# Revit family: 706510001_Dispensador de Toallas
name_source: partatom
category: Generic Models
units: mm (PartAtom-declared; Revit-internal decimal feet)

## family parameters
Always vertical = Yes
Can host rebar = No
Cut with Voids When Loaded = No
Host = Wall
OmniClass Number = 23.31.25.19.13
OmniClass Title = Paper Towel Dispenser With Disposal Units
Part Type = Normal
Room Calculation Point = No
Round Connector Dimension = Use Diameter
Shared = No

## types (1)
- Ref. 706510001 Dispensador de Toallas
    Acabado = Cromado
    Alto = 260 mm  [stored 0.853018 ft]
    Ancho = 282 mm  [stored 0.925197 ft]
    Años de Garantía = 1 año
    Capacidad de toallas doblez sencillo = 150
    Capacidad de toallas pleglables = 200
    Creado por = IDD
    Description = Tamaño ajustado para adecuar en diferentes baños
• Visor de nivel de toallas para abastecimiento.
• Cerradura de llave (incluye juegos para mantenimiento).
• Sistema de fijación extrema, ideal para instituciones de alto tráfico.
• Fabricación en acero inoxidable ofreciendo mayor calidad y servicio.
    Dimensiones generales del producto = Largo (cm) 280 ancho (cm)
102 alto (cm) 248.
    Fecha de creación = 22/07/2020
    Garantía Acabados = 3 años
    Manufacturer = Corona
    Material = Corona_Acero inoxidable
    Peso Bruto aprox = 1,660 g 3.6597 lb
    Peso Neto aprox = 1,480 g 3.262844142 lb.
    Profundidad = 102 mm
    Tipología = Dispensador
    URL = https://corona.co

note: [stored X ft] marks values corroborated as IEEE doubles in the binary element streams (Revit-internal decimal feet)

## geometry (parser evidence)
native form markers: Blend x3, Extrusion x1, Sweep x5
no freeform markers — native parametric forms only
